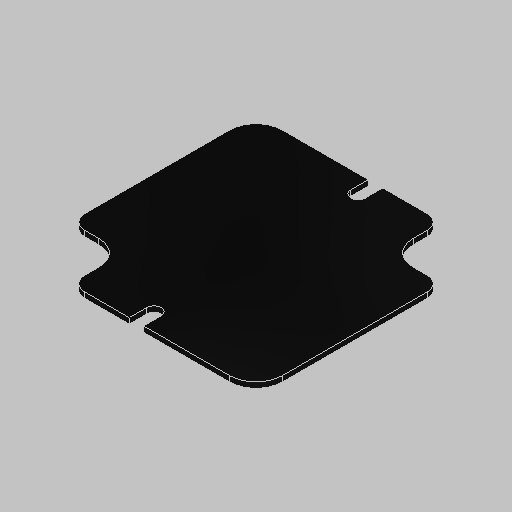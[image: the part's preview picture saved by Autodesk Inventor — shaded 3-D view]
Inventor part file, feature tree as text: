
AUTODESK INVENTOR PART (.ipt)
format: ipt  version: 2023.5 (Build 275446000, 446)  size: 76,800 bytes
history: native  units: mm (DEFAULTED — no unit token found)
features: fillet x1
ambient origin geometry x8: Origin, YZ Plane, XZ Plane, XY Plane, X Axis, Y Axis, Z Axis, Center Point
bodies: Solid1 (feature_tree)
feature tree (1):
  fillet  "Fillet2"  [1 undecoded]
note: 1 required parameter value undecoded (feature->parameter linkage not recoverable at this tier; creation-order binding heuristic only, values carry confidence <= 0.55)
